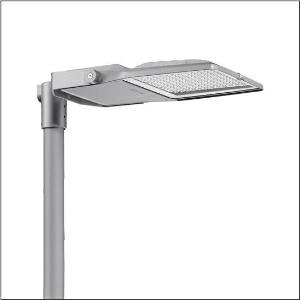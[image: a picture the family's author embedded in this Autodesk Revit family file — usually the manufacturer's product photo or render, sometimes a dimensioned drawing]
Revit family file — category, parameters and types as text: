
# Revit family: floodlight_fl_21_iq_midi___pl61_5xa7782f4c3a_0871
name_source: partatom
category: Lighting Fixtures
units: mm (PartAtom-declared; Revit-internal decimal feet)

## family parameters
Cut with Voids When Loaded = No
Host = Face
Light Source = No
Part Type = Normal
Room Calculation Point = No
Round Connector Dimension = Use Diameter
Shared = No

## types (1)
- --- (1 x LED, 36650 lm, 270.2 W, 4000K)
    Apparent Load = 270 VA
    CIE Flux Codes = 33 65 98 100 100
    Color Rendering = 70
    Color Temperature = 4000K
    Default Elevation = 1800 mm
    Description = Floodlight FL 21 iQ midi, floodlight, primary light control with lens, of PMMA, primary optical cover: protective disc, of toughened safety glass, transparent, light distribution: PL61, light emission: direct distribution, installation type: surface-mounted, LED, High Power LED, rated luminous flux: 36.650lm, luminous efficacy: 136lm/W, light colour: 740, colour temperature: 4000K, control gear: ECG iQ, control: optimised constant luminous flux control (CLO 2.0), Desk-Remote (wireless, voltage-free reading and setting of iQ features in the workshop via application-optimized NFC function/RFID function), Smart-Wire, Night-Set, Temp-Guard, Auto-Match, Street-Remote, with terminal, 6-pole, mains connection: 220..240V, AC, 50/60Hz, start of lifetime: 270W, end of service life: 287W, reduction: 118W, luminaire housing, of diecast aluminium, powder-coated, Siteco® metallic grey (DB 702S), corrosivity category C5 mid according to DIN EN ISO 12944, sealing non-destructively replaceable, please order mast flange separately, mast bracket, of steel, galvanised, powder-coated, Siteco® metallic grey (DB 702S), protection rating (complete): IP66, insulation class (complete): insulation class II (safety insulation), certification: CE, protection symbol: D, impact resistance: IK08, permissible operating ambient temperature: -40..+40°C, permissible operating ambient temperature for outdoor applications: -40..+50°C, standard: DIN EN 12944, LABS conformity tested according to VDMA 24364:2018-05, packaging unit: 1 piece

Light Distribution: PL61
    Height = 76 mm
    Lamp = 1 x LED
    Lamp Light Flux = 36650 lm
    Lamp Power = 270.2 W
    Lamp count = 1
    Length = 657 mm
    Luminous efficacy = 136 lm/W
    Manufacturer = Siteco
    ModVariant = No
    Model = 5XA7782F4C3A
    Number of Poles = 1
    OnlyDefault = Yes
    Power Factor = 1
    Product Name = Floodlight FL 21 iQ midi | PL61
    Product group = floodlight | pylon annexe
    ProductGroupID = 6200
    Protection Class = Protection class II
    Protection Degree = IP 66
    RLX_Detail_Level = 1
    RLX_Emergency_Light_Flux = 0 lm
    RLX_Emergency_Type = 0
    RLX_Emergency_Type_DB = No
    RlxData = <blob elided: 153717 chars, md5=f8c82b6b>
    Socket = socket
    Standby Power = 0 W
    System Light Flux = 36650 lm
    System Power = 270 W
    Type Comments = factory setting: luminous flux: 100 % | dim-lin: 254 | 620 mA
    Type Image = l_1007123.jpg
    URL = http://relux.com
    VarID = @adj_056469
    Voltage = 0 V
    Weight = 0.00 kg
    Width = 442 mm

## geometry (parser evidence)
native form markers: Blend x4, Sweep x14
no freeform markers — native parametric forms only
